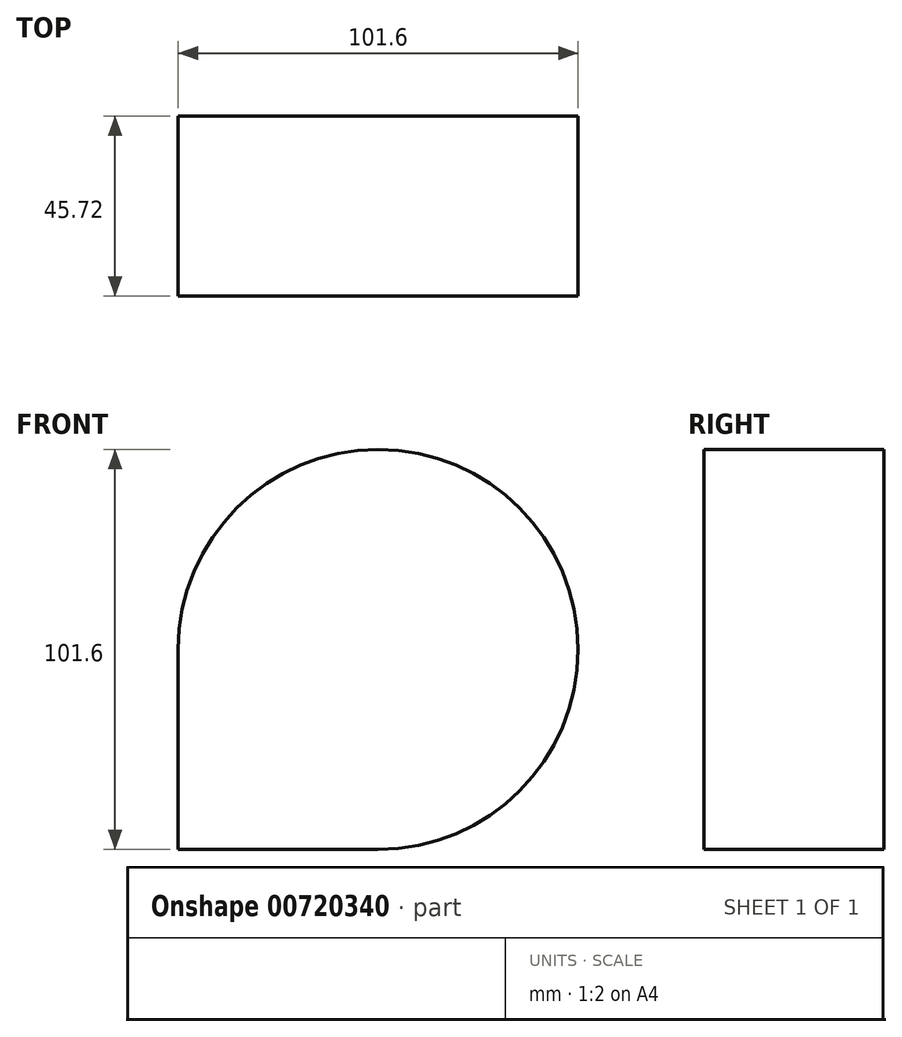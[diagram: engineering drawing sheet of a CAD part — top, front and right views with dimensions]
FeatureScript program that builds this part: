
annotation { "Feature Type Name" : "Feature", "Feature Type Description" : "" }
export const myFeature = defineFeature(function(context is Context, id is Id, definition is map)
    precondition{}
    {
        {
            var Q0;
            Q0=qCreatedBy(makeId("Front.planeOp"),FACE);
            var sketch = newSketch(context, id + "F0", { "sketchPlane" : qUnion([Q0])});
            skLineSegment(sketch, "E0", {"start": v(-72.26, 50.8) * mm, "end": v(-21.46, 50.8) * mm});
            skLineSegment(sketch, "E1", {"start": v(-21.46, 50.8) * mm, "end": v(-21.46, 0) * mm});
            skLineSegment(sketch, "E2", {"start": v(-72.26, 50.8) * mm, "end": v(-72.26, 0) * mm});
            skLineSegment(sketch, "E3", {"start": v(-72.26, 0) * mm, "end": v(-21.46, 0) * mm});
            skSolve(sketch);
        }
        {
            var Q0;
            Q0 = qSketchRegion(id + "F0", true);
            extrude(context, id + "F1", {"entities" : qUnion([Q0]), "depth" : 45.72 * mm, "offsetDistance" : 25.4 * mm});
        }
        {
            var Q0;
            Q0=makeQuery(id+"F1.opExtrude","SWEPT_FACE",FACE,{"disambiguationData":[OSD([sQuery(id+"F0.wireOp",EDGE,"E0")])]});
            var Q1;
            Q1=makeQuery(id+"F1.opExtrude","SWEPT_EDGE",EDGE,{"disambiguationData":[OSD([sQuery(id+"F0.wireOp",EDGE,"E0"),sQuery(id+"F0.wireOp",EDGE,"E1")])]});
            revolve(context, id + "F2", {"operationType" : NewBodyOperationType.ADD, "surfaceOperationType" : NewSurfaceOperationType.NEW, "entities" : qUnion([Q0]), "axis" : qUnion([Q1]), "revolveType" : RevolveType.FULL});
        }
    });
